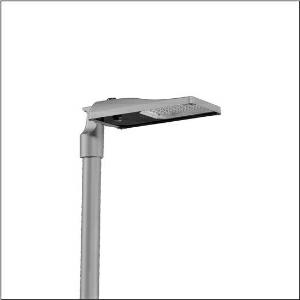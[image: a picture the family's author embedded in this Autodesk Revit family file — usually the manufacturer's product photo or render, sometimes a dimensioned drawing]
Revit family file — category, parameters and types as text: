
# Revit family: streetlight_sl_31_mini___st0_5a_5xh2b4at08ha_3879
name_source: partatom
category: Lighting Fixtures
units: mm (PartAtom-declared; Revit-internal decimal feet)

## family parameters
Cut with Voids When Loaded = No
Host = Face
Light Source = No
Part Type = Normal
Room Calculation Point = No
Round Connector Dimension = Use Diameter
Shared = No

## types (1)
- --- (1 x LED, 9560 lm, 68.3 W, 4000K)
    Apparent Load = 68 VA
    CIE Flux Codes = 41 75 97 100 100
    Color Rendering = 70
    Color Temperature = 4000K
    Default Elevation = 1800 mm
    Description = Streetlight SL 31 mini D4i mast luminaire for post-top, side-entry; light control with lens of PMMA; light distribution: ST0.5a, direct asymmetric distribution, for standard-compliant lighting for roads and squares; LED: luminous flux: 9.560lm, light colour: 740, colour temperature: 4000K; luminous efficacy: 140,2lm/W; control: pre-setting: logarithmic dimming characteristic, flexible luminous flux parameterisation, time-dependent luminous flux control, constant luminous flux control, power reduction, intelligent temperature release in ECG and LED module, overheat protection; luminaire housing, of diecast aluminium, Siteco® metallic grey (DB 702S), corrosivity category C5 high according to DIN EN ISO 12944; cover of toughened safety glass, transparent, mast flange of diecast aluminium, Siteco® metallic grey (DB 702S), spigot size: 76/60mm, mast flange included unmounted; with cable H07RN-F 2x 1.5mm², cable length: 8,5m, connection cable pre-assembled; mains connection: 220..240V, AC, 50/60Hz; power consumption (at start of service life): 68,2W / (at end of service life): 74,4W / (with reduced operation 50%): 29,7W; protection rating (complete): IP66; insulation class (complete): insulation class II (safety insulation); impact resistance: IK09; certification: CE, ENEC, ENEC+, VDE, UKCA, ZD4i; permissible operating ambient temperature for outdoor applications: -40..+50°C; packaging unit: 1 piece

Light Distribution: ST0.5a
    Height = 76 mm
    Lamp = 1 x LED
    Lamp Light Flux = 9560 lm
    Lamp Power = 68.3 W
    Lamp count = 1
    Length = 547 mm
    Luminous efficacy = 140 lm/W
    Manufacturer = Siteco
    ModVariant = No
    Model = 5XH2B4AT08HA
    Number of Poles = 1
    OnlyDefault = Yes
    Power Factor = 1
    Product Name = Streetlight SL 31 mini | ST0.5a
    Product group = mast luminaire | pylon top
    ProductGroupID = 6100
    Protection Class = Protection class II
    Protection Degree = IP 66
    RLX_Detail_Level = 1
    RLX_Emergency_Light_Flux = 0 lm
    RLX_Emergency_Type = 0
    RLX_Emergency_Type_DB = No
    RlxData = <blob elided: 35273 chars, md5=8646d6f7>
    Socket = socket
    Standby Power = 0 W
    System Light Flux = 9560 lm
    System Power = 68 W
    Type Comments = factory setting: luminous flux: 100 % | dim-lin: 254 | 692 mA
    Type Image = l_1300332.jpg
    URL = http://relux.com
    VarID = @adj_003071
    Voltage = 0 V
    Weight = 0.00 kg
    Width = 265 mm

## geometry (parser evidence)
native form markers: Blend x4, Sweep x10
no freeform markers — native parametric forms only
